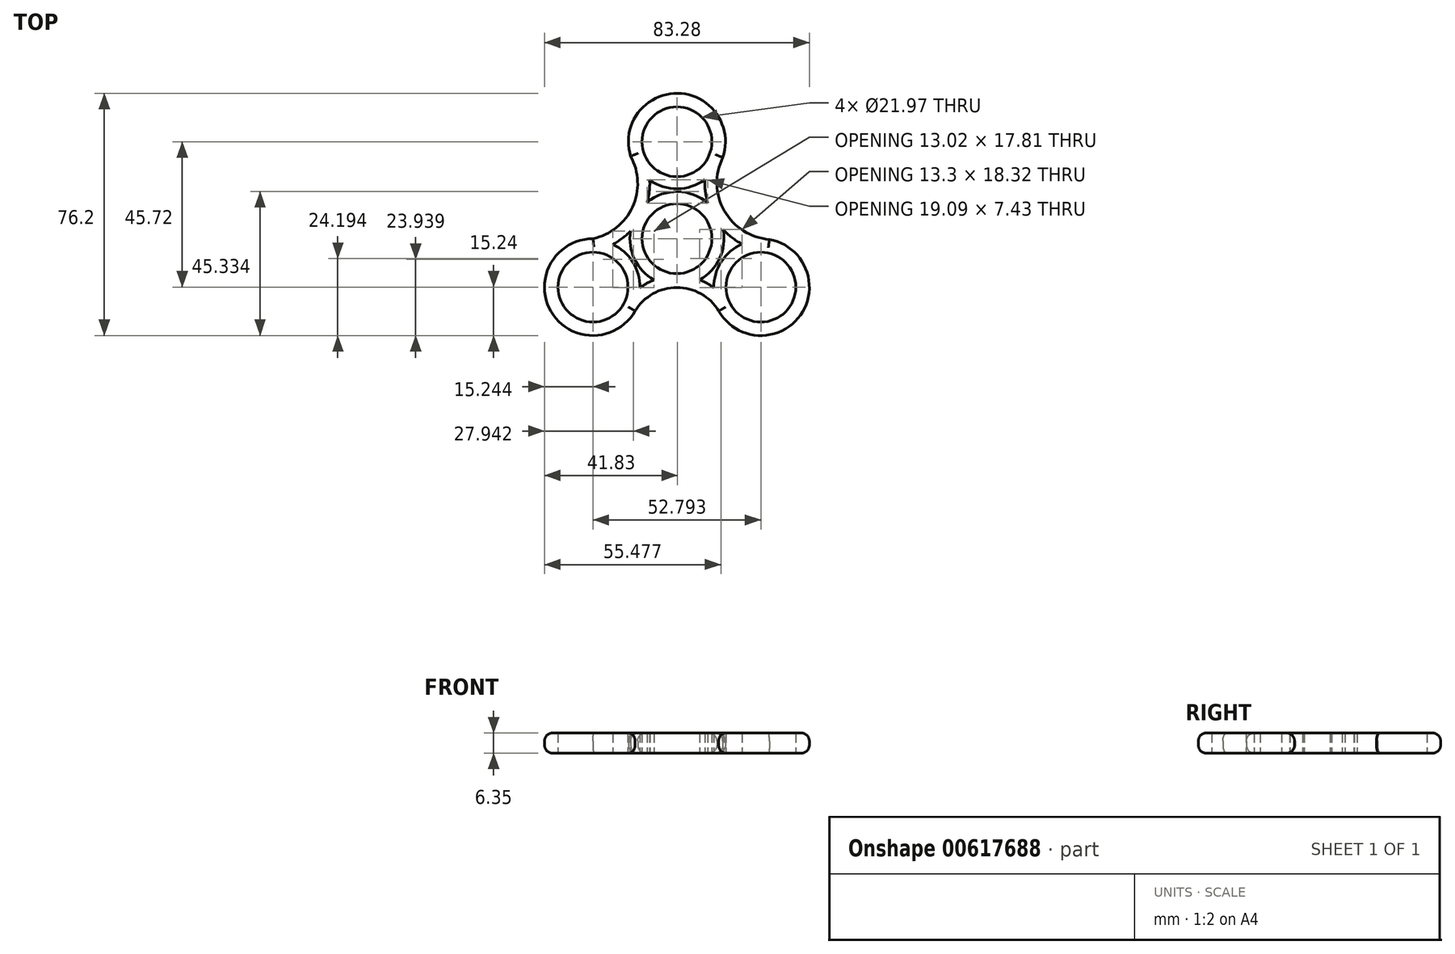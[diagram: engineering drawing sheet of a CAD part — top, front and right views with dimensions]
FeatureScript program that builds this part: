
annotation { "Feature Type Name" : "Feature", "Feature Type Description" : "" }
export const myFeature = defineFeature(function(context is Context, id is Id, definition is map)
    precondition{}
    {
        {
            var Q0;
            Q0=qCreatedBy(makeId("Top.planeOp"),FACE);
            var sketch = newSketch(context, id + "F0", { "sketchPlane" : qUnion([Q0])});
            skCircle(sketch, "E0", {"center": v(0, 0) * mm, "radius": 10.99 * mm});
            skLineSegment(sketch, "E1", {"start": v(0, 0) * mm, "end": v(0, 30.48) * mm});
            skLineSegment(sketch, "E2", {"start": v(0, 0) * mm, "end": v(-26.4, -15.24) * mm});
            skLineSegment(sketch, "E3", {"start": v(0, 0) * mm, "end": v(26.4, -15.24) * mm});
            skCircle(sketch, "E4", {"center": v(0, 30.48) * mm, "radius": 10.99 * mm});
            skCircle(sketch, "E5", {"center": v(26.4, -15.24) * mm, "radius": 10.99 * mm});
            skCircle(sketch, "E6", {"center": v(-26.4, -15.24) * mm, "radius": 10.99 * mm});
            skCircle(sketch, "E7", {"center": v(0, 30.48) * mm, "radius": 15.24 * mm});
            skCircle(sketch, "E8", {"center": v(26.4, -15.24) * mm, "radius": 15.24 * mm});
            skCircle(sketch, "E9", {"center": v(-26.4, -15.24) * mm, "radius": 15.24 * mm});
            skCircle(sketch, "E10", {"center": v(0, 0) * mm, "radius": 15.24 * mm});
            skArc(sketch, "E11", {"start": v(-26.4, 0) * mm, "mid": v(-13.96, 9.97) * mm, "end": v(-14.54, 25.9) * mm});
            skArc(sketch, "E12", {"start": v(14.4, 25.51) * mm, "mid": v(14.91, 8.74) * mm, "end": v(29.08, -0.24) * mm});
            skArc(sketch, "E13", {"start": v(13.13, -22.75) * mm, "mid": v(0, -15.34) * mm, "end": v(-13.13, -22.75) * mm});
            skArc(sketch, "E14", {"start": v(-26.4, 0) * mm, "mid": v(-18.8, 12.19) * mm, "end": v(-14.54, 25.9) * mm});
            skArc(sketch, "E15", {"start": v(14.4, 25.51) * mm, "mid": v(19.3, 11.25) * mm, "end": v(29.08, -0.24) * mm});
            skArc(sketch, "E16", {"start": v(13.13, -22.75) * mm, "mid": v(0, -20.14) * mm, "end": v(-13.13, -22.75) * mm});
            skSolve(sketch);
        }
        {
            var Q0;
            {var subQ0=sQuery(id+"F0.wireOp",EDGE,"E12");var subQ1=sQuery(id+"F0.wireOp",EDGE,"E7");var subQ2=makeQuery(id+"F0.imprint","INTERSECT",VERTEX,{"derivedFrom":[subQ1,subQ0]});Q0=makeQuery(id+"F0.imprint","IMPRINT",FACE,{"disambiguationData":[TD([[makeQuery(id+"F0.imprint","IMPRINT",EDGE,{"disambiguationData":[TD([[subQ2,-1.0]])],"derivedFrom":subQ0}),-1.0]])]});}
            var Q1;
            {var subQ0=sQuery(id+"F0.wireOp",EDGE,"E12");var subQ1=sQuery(id+"F0.wireOp",EDGE,"E8");var subQ2=makeQuery(id+"F0.imprint","INTERSECT",VERTEX,{"derivedFrom":[subQ1,subQ0]});Q1=makeQuery(id+"F0.imprint","IMPRINT",FACE,{"disambiguationData":[TD([[makeQuery(id+"F0.imprint","IMPRINT",EDGE,{"disambiguationData":[TD([[subQ2,1.0]])],"derivedFrom":subQ0}),-1.0]])]});}
            var Q2;
            {var subQ1=sQuery(id+"F0.wireOp",EDGE,"E0");var subQ5=sQuery(id+"F0.wireOp",EDGE,"E1");var subQ6=makeQuery(id+"F0.imprint","INTERSECT",VERTEX,{"derivedFrom":[subQ1,subQ5]});Q2=makeQuery(id+"F0.imprint","IMPRINT",FACE,{"disambiguationData":[TD([[makeQuery(id+"F0.imprint","IMPRINT",EDGE,{"disambiguationData":[TD([[subQ6,1.0]])],"derivedFrom":subQ1}),-1.0]])]});}
            var Q3;
            {var subQ0=sQuery(id+"F0.wireOp",EDGE,"E2");var subQ1=sQuery(id+"F0.wireOp",EDGE,"E0");var subQ2=makeQuery(id+"F0.imprint","INTERSECT",VERTEX,{"derivedFrom":[subQ1,subQ0]});Q3=makeQuery(id+"F0.imprint","IMPRINT",FACE,{"disambiguationData":[TD([[makeQuery(id+"F0.imprint","IMPRINT",EDGE,{"disambiguationData":[TD([[subQ2,1.0]])],"derivedFrom":subQ1}),-1.0]])]});}
            var Q4;
            {var subQ0=sQuery(id+"F0.wireOp",EDGE,"E11");Q4=makeQuery(id+"F0.imprint","IMPRINT",FACE,{"disambiguationData":[TD([[makeQuery(id+"F0.imprint","IMPRINT",EDGE,{"derivedFrom":subQ0}),-1.0]])]});}
            var Q5;
            Q5=makeQuery(id+"F0.imprint","IMPRINT",FACE,{"disambiguationData":[TD([[makeQuery(id+"F0.imprint","IMPRINT",EDGE,{"derivedFrom":sQuery(id+"F0.wireOp",EDGE,"E4")}),-1.0]])]});
            var Q6;
            {var subQ0=sQuery(id+"F0.wireOp",EDGE,"E13");Q6=makeQuery(id+"F0.imprint","IMPRINT",FACE,{"disambiguationData":[TD([[makeQuery(id+"F0.imprint","IMPRINT",EDGE,{"derivedFrom":subQ0}),-1.0]])]});}
            var Q7;
            {var subQ0=sQuery(id+"F0.wireOp",EDGE,"E2");var subQ1=sQuery(id+"F0.wireOp",EDGE,"E0");var subQ2=makeQuery(id+"F0.imprint","INTERSECT",VERTEX,{"derivedFrom":[subQ1,subQ0]});Q7=makeQuery(id+"F0.imprint","IMPRINT",FACE,{"disambiguationData":[TD([[makeQuery(id+"F0.imprint","IMPRINT",EDGE,{"disambiguationData":[TD([[subQ2,-1.0]])],"derivedFrom":subQ1}),-1.0]])]});}
            var Q8;
            Q8=makeQuery(id+"F0.imprint","IMPRINT",FACE,{"disambiguationData":[TD([[makeQuery(id+"F0.imprint","IMPRINT",EDGE,{"derivedFrom":sQuery(id+"F0.wireOp",EDGE,"E5")}),-1.0]])]});
            var Q9;
            Q9=makeQuery(id+"F0.imprint","IMPRINT",FACE,{"disambiguationData":[TD([[makeQuery(id+"F0.imprint","IMPRINT",EDGE,{"derivedFrom":sQuery(id+"F0.wireOp",EDGE,"E6")}),-1.0]])]});
            extrude(context, id + "F1", {"entities" : qUnion([Q0, Q1, Q2, Q3, Q4, Q5, Q6, Q7, Q8, Q9]), "depth" : 6.35 * mm, "offsetDistance" : 25.4 * mm});
        }
        {
            var Q0;
            Q0=makeQuery(id+"F1.opExtrude","CAP_EDGE",EDGE,{"disambiguationData":[OSD([sQuery(id+"F0.wireOp",EDGE,"E7")])],"isStart":false});
            var Q1;
            Q1=makeQuery(id+"F1.opExtrude","CAP_EDGE",EDGE,{"disambiguationData":[OSD([sQuery(id+"F0.wireOp",EDGE,"E11")])],"isStart":false});
            var Q2;
            Q2=makeQuery(id+"F1.opExtrude","CAP_EDGE",EDGE,{"disambiguationData":[OSD([sQuery(id+"F0.wireOp",EDGE,"E12")])],"isStart":false});
            var Q3;
            Q3=makeQuery(id+"F1.opExtrude","CAP_EDGE",EDGE,{"disambiguationData":[OSD([sQuery(id+"F0.wireOp",EDGE,"E13")])],"isStart":false});
            var Q4;
            Q4=makeQuery(id+"F1.opExtrude","CAP_EDGE",EDGE,{"disambiguationData":[OSD([sQuery(id+"F0.wireOp",EDGE,"E8")])],"isStart":false});
            var Q5;
            Q5=makeQuery(id+"F1.opExtrude","CAP_EDGE",EDGE,{"disambiguationData":[OSD([sQuery(id+"F0.wireOp",EDGE,"E9")])],"isStart":false});
            fillet(context, id + "F2", {"entities" : qUnion([Q0, Q1, Q2, Q3, Q4, Q5]), "radius" : 2.54 * mm, "tangentPropagation" : true, "allowEdgeOverflow" : false});
        }
        {
            var Q0;
            Q0=makeQuery(id+"F1.opExtrude","CAP_EDGE",EDGE,{"disambiguationData":[OSD([sQuery(id+"F0.wireOp",EDGE,"E13")])],"isStart":true});
            var Q1;
            Q1=makeQuery(id+"F1.opExtrude","CAP_EDGE",EDGE,{"disambiguationData":[OSD([sQuery(id+"F0.wireOp",EDGE,"E8")])],"isStart":true});
            var Q2;
            Q2=makeQuery(id+"F1.opExtrude","CAP_EDGE",EDGE,{"disambiguationData":[OSD([sQuery(id+"F0.wireOp",EDGE,"E12")])],"isStart":true});
            var Q3;
            Q3=makeQuery(id+"F1.opExtrude","CAP_EDGE",EDGE,{"disambiguationData":[OSD([sQuery(id+"F0.wireOp",EDGE,"E9")])],"isStart":true});
            var Q4;
            Q4=makeQuery(id+"F1.opExtrude","CAP_EDGE",EDGE,{"disambiguationData":[OSD([sQuery(id+"F0.wireOp",EDGE,"E7")])],"isStart":true});
            var Q5;
            Q5=makeQuery(id+"F1.opExtrude","CAP_EDGE",EDGE,{"disambiguationData":[OSD([sQuery(id+"F0.wireOp",EDGE,"E11")])],"isStart":true});
            fillet(context, id + "F3", {"entities" : qUnion([Q0, Q1, Q2, Q3, Q4, Q5]), "radius" : 2.54 * mm, "tangentPropagation" : true, "allowEdgeOverflow" : false});
        }
        {
            var Q0;
            Q0=makeQuery(id+"F1.opExtrude","CAP_FACE",FACE,{"disambiguationData":[OSD([sQuery(id+"F0.wireOp",EDGE,"E0"),sQuery(id+"F0.wireOp",EDGE,"E4"),sQuery(id+"F0.wireOp",EDGE,"E5"),sQuery(id+"F0.wireOp",EDGE,"E6"),sQuery(id+"F0.wireOp",EDGE,"E7"),sQuery(id+"F0.wireOp",EDGE,"E8"),sQuery(id+"F0.wireOp",EDGE,"E9"),sQuery(id+"F0.wireOp",EDGE,"E11"),sQuery(id+"F0.wireOp",EDGE,"E12"),sQuery(id+"F0.wireOp",EDGE,"E13")])],"isStart":true});
            var Q1;
            Q1=makeQuery(id+"F1.opExtrude","CAP_FACE",FACE,{"disambiguationData":[OSD([sQuery(id+"F0.wireOp",EDGE,"E0"),sQuery(id+"F0.wireOp",EDGE,"E4"),sQuery(id+"F0.wireOp",EDGE,"E5"),sQuery(id+"F0.wireOp",EDGE,"E6"),sQuery(id+"F0.wireOp",EDGE,"E7"),sQuery(id+"F0.wireOp",EDGE,"E8"),sQuery(id+"F0.wireOp",EDGE,"E9"),sQuery(id+"F0.wireOp",EDGE,"E11"),sQuery(id+"F0.wireOp",EDGE,"E12"),sQuery(id+"F0.wireOp",EDGE,"E13")])],"isStart":false});
            shell(context, id + "F4", {"entities" : qUnion([Q0, Q1]), "thickness" : 3.8 * mm});
        }
    });
